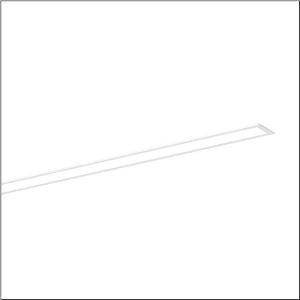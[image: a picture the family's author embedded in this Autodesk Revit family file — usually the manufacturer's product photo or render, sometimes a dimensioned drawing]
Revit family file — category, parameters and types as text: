
# Revit family: silica_r__21_51mx10da42wb_084b
name_source: partatom
category: Lighting Fixtures
units: mm (PartAtom-declared; Revit-internal decimal feet)

## family parameters
Cut with Voids When Loaded = No
Host = Face
Light Source = No
Part Type = Normal
Room Calculation Point = No
Round Connector Dimension = Use Diameter
Shared = No

## types (1)
- --- (1 x LED, 2400 lm, 15.2 W, 4000K)
    Apparent Load = 15 VA
    CIE Flux Codes = 48 79 96 100 100
    Color Rendering = 80
    Color Temperature = 4000K
    Default Elevation = 1800 mm
    Description = Silica® 21, office luminaire, primary optical cover: cover, of PMMA, opal, light emission: direct distribution, primary light characteristic: symmetric, installation type: recessed, LED, rated luminous flux: 2.400lm, luminous efficacy: 158lm/W, light colour: 840, colour temperature: 4000K, with terminal, 3+2-pole, max. 2.5mm², mains connection: 220..240V, AC, 50/60Hz, rated input power: 15.2W, luminaire housing, of aluminium, traffic white (RAL 9016), length: 1.228mm, width: 79mm, height: 53mm, protection rating (complete): IP20, insulation class (complete): insulation class I (protective earthing), certification: CE, permissible operating ambient temperature: 0..+35°C, standard: EN 50419, packaging unit: 1 piece
    Height = 0 mm  [stored 0 ft]
    Lamp = 1 x LED
    Lamp Light Flux = 2400 lm
    Lamp Power = 15.2 W
    Lamp count = 1
    Length = 1227 mm
    Luminous efficacy = 158 lm/W
    Manufacturer = Siteco
    ModVariant = No
    Model = 51MX10DA42WB
    Mounting Place = Ceiling
    Mounting Type = Recessed
    Number of Poles = 1
    OnlyDefault = Yes
    Power Factor = 1
    Product Name = Silica® 21
    Product group = office luminaire | ceiling recessed
    ProductGroupID = 401
    Protection Class = Protection class I
    Protection Degree = IP 20
    RLX_Detail_Level = 1
    RLX_Emergency_Light_Flux = 0 lm
    RLX_Emergency_Type = 0
    RLX_Emergency_Type_DB = No
    RlxData = <blob elided: 21013 chars, md5=078f9d8c>
    Socket = socket
    Standby Power = 0 W
    System Light Flux = 2400 lm
    System Power = 15 W
    Type Comments = factory setting: luminous flux: 100 % | dim-lin: 254 | 218 mA
    Type Image = l_1297737.jpg
    URL = http://relux.com
    VarID = @adj_047797
    Voltage = 0 V
    Weight = 0.00 kg
    Width = 79 mm

note: [stored X ft] marks values corroborated as IEEE doubles in the binary element streams (Revit-internal decimal feet)

## geometry (parser evidence)
native form markers: Blend x4, Sweep x10
no freeform markers — native parametric forms only
